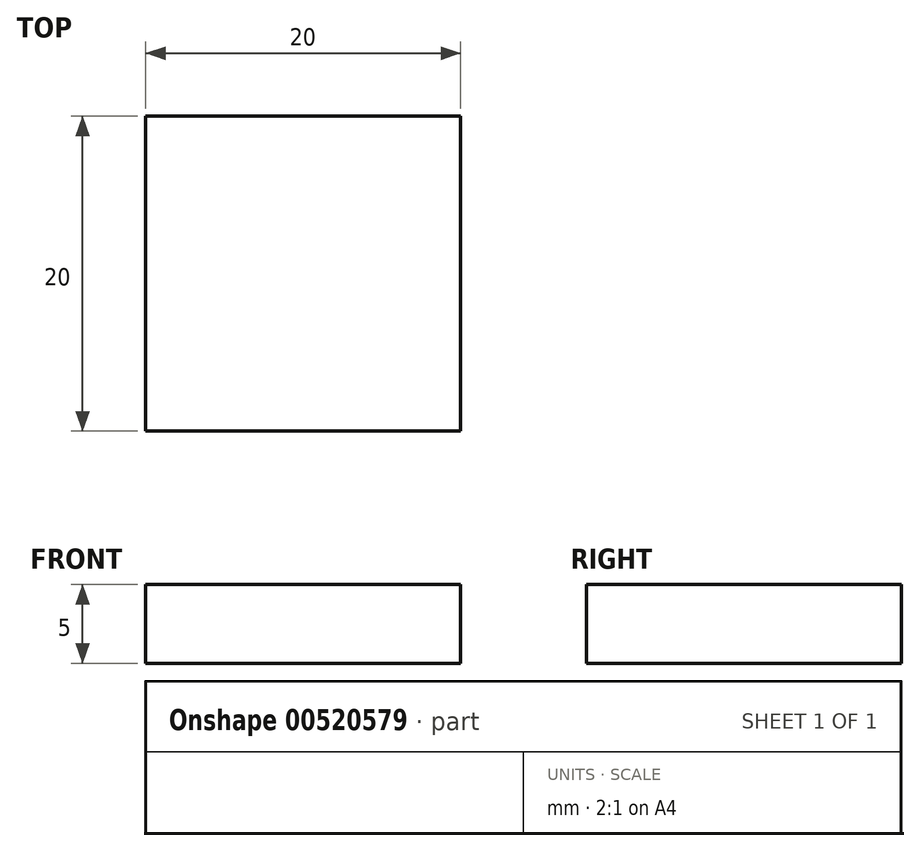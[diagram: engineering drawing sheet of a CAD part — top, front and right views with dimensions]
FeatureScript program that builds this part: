
annotation { "Feature Type Name" : "Feature", "Feature Type Description" : "" }
export const myFeature = defineFeature(function(context is Context, id is Id, definition is map)
    precondition{}
    {
        {
            var Q0;
            Q0=qCreatedBy(makeId("Top.planeOp"),FACE);
            var sketch = newSketch(context, id + "F0", { "sketchPlane" : qUnion([Q0])});
            skLineSegment(sketch, "E0.bottom", {"start": v(0, 0) * mm, "end": v(20, 0) * mm});
            skLineSegment(sketch, "E0.top", {"start": v(0, 20) * mm, "end": v(20, 20) * mm});
            skLineSegment(sketch, "E0.left", {"start": v(0, 0) * mm, "end": v(0, 20) * mm});
            skLineSegment(sketch, "E0.right", {"start": v(20, 0) * mm, "end": v(20, 20) * mm});
            skSolve(sketch);
        }
        {
            var Q0;
            Q0=makeQuery(id+"F0.imprint","IMPRINT",FACE,{"disambiguationData":[TD([[makeQuery(id+"F0.imprint","IMPRINT",EDGE,{"derivedFrom":sQuery(id+"F0.wireOp",EDGE,"E0.bottom")}),1.0]])]});
            extrude(context, id + "F1", {"entities" : qUnion([Q0]), "depth" : 5 * mm, "offsetDistance" : 25 * mm});
        }
    });
